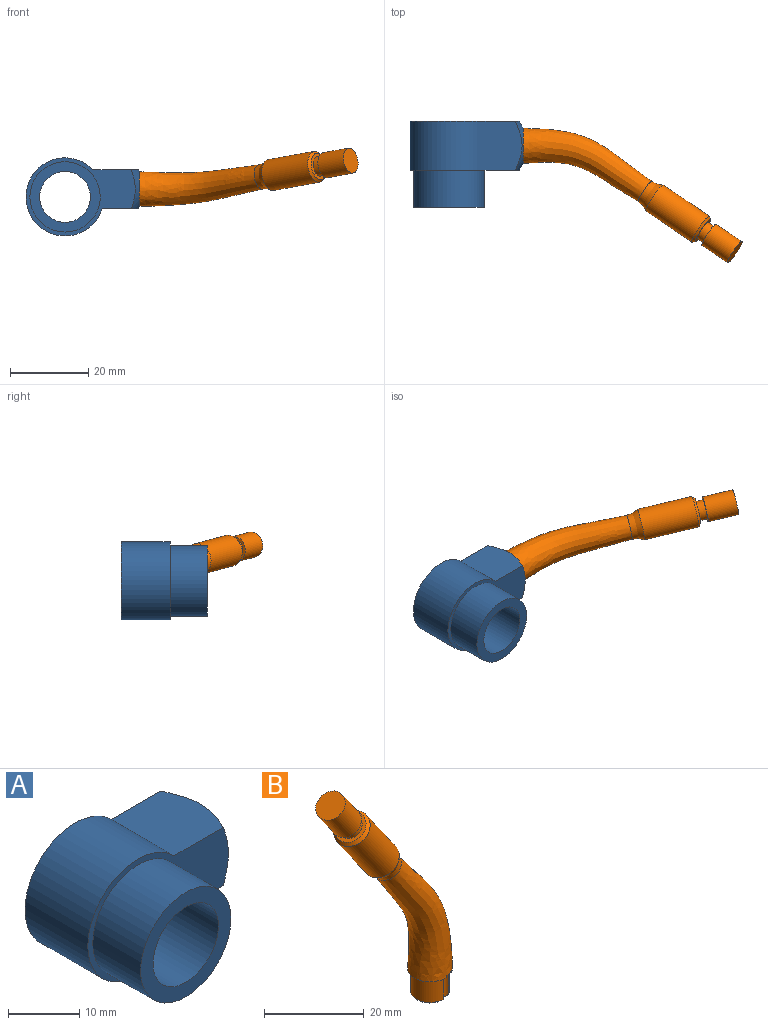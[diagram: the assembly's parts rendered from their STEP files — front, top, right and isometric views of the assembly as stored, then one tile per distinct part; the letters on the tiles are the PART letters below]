
ASSEMBLY  parts=2 mates=1
PART A: 12 faces, bbox 29x23.8x20 mm
  f0: plane 9x9mm, normal (1,0,0), area 13.4mm2, adj f1,f3
  f1: cylinder r=4mm len=8mm, axis (1,0,0), area 163.4mm2, adj f0,f2
  f2: plane 8x8mm, normal (1,0,0), area 50.3mm2, adj f1
  f3: cone r=9.5mm half-angle=60deg, axis (-1,0,0), area 70.9mm2, adj f0,f8,f9,f10,f11
  f4: plane 18x18mm, normal (0,-1,0), area 121.7mm2, adj f5,f7
  f5: cylinder r=9mm len=18mm, axis (0,1,0), area 537.2mm2, adj f4,f9
  f6: cylinder r=10mm len=20mm, axis (0,1,0), area 650.4mm2, adj f8,f9,f10,f11
  f7: cylinder r=6.5mm len=22mm, axis (0,-1,0), area 898.5mm2, adj f4,f8
  f8: plane 27.99x20mm, normal (0,1,0), area 264.5mm2, adj f3,f6,f7,f10,f11
  f9: plane 27.99x20mm, normal (0,-1,0), area 142.7mm2, adj f3,f5,f6,f10,f11
  f10: plane 12.5x9.17mm, normal (0,0,-1), area 106.7mm2, adj f3,f6,f8,f9
  f11: plane 12.5x11.57mm, normal (0,0,1), area 136.7mm2, adj f3,f6,f8,f9
PART B: 17 faces, bbox 35.4x9x62.1 mm
  f0: plane 9x9mm, normal (0,0,-1), area 14.6mm2, adj f1,f3,f7,f8
  f1: bspline ~33.02x19.2mm, area 826.8mm2, adj f0,f7,f8,f9,f11
  f2: cylinder r=1mm len=6.5mm, axis (0,0,1), area 18.5mm2, adj f3,f4,f7,f8,f9,f12
  f3: cylinder r=3.9mm len=7.8mm, axis (0,0,1), area 123.7mm2, adj f0,f2,f12
  f4: plane 6.8x6.8mm, normal (0,0,-1), area 35.8mm2, adj f2,f12
  f5: plane 6.75x5.53mm, normal (-0.57,0,0.82), area 16.1mm2, adj f10,f13
  f6: cylinder r=4mm len=16.36mm, axis (0.57,0,-0.82), area 361.3mm2, adj f10,f11
  f7: plane 0.6x0.5mm, normal (-0.97,-0.26,0), area 0.3mm2, adj f0,f1,f2,f9
  f8: plane 0.6x0.5mm, normal (0.97,0.26,0), area 0.3mm2, adj f0,f1,f2,f9
  f9: plane 2.09x1.72mm, normal (0,0,-1), area 2.7mm2, adj f1,f2,f7,f8
  f10: cone r=3.38mm half-angle=45deg, axis (0.57,0,-0.82), area 20.5mm2, adj f5,f6
  f11: bspline ~8x7.57mm, area 68.6mm2, adj f1,f6
  f12: cone r=3.4mm half-angle=45deg, axis (0,0,1), area 14.9mm2, adj f2,f3,f4
  f13: cylinder r=2.5mm len=5.24mm, axis (0.57,0,-0.82), area 31.4mm2, adj f5,f14
  f14: plane 6.5x5.32mm, normal (0.57,0,-0.82), area 13.5mm2, adj f13,f15
  f15: cylinder r=3.25mm len=10.28mm, axis (0.57,0,-0.82), area 163.4mm2, adj f14,f16
  f16: plane 6.5x5.32mm, normal (-0.57,0,0.82), area 33.2mm2, adj f15
PLACE A at identity fixed
PLACE B rot(axis=(0.52,0.68,0.52),111.8deg) t=(19,0,2)mm
MATE fastened B.f3 <-> A.f1  axis (-1,0,0) through (19,0,2)mm
